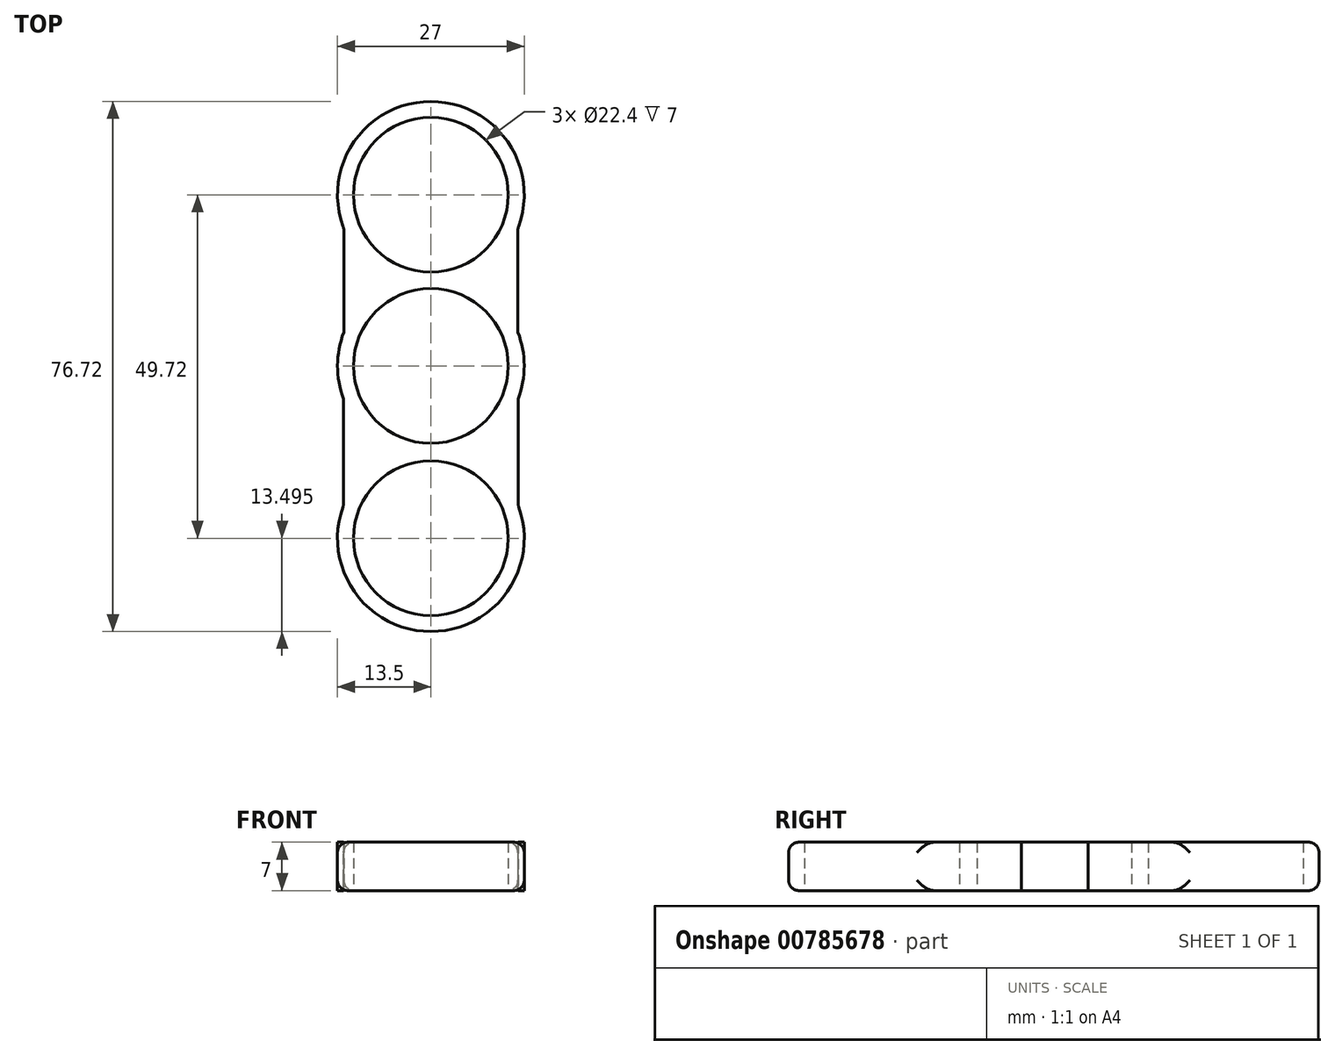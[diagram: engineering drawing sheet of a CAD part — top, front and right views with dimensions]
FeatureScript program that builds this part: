
annotation { "Feature Type Name" : "Feature", "Feature Type Description" : "" }
export const myFeature = defineFeature(function(context is Context, id is Id, definition is map)
    precondition{}
    {
        {
            var Q0;
            Q0=qCreatedBy(makeId("Top.planeOp"),FACE);
            var sketch = newSketch(context, id + "F0", { "sketchPlane" : qUnion([Q0])});
            skCircle(sketch, "E0", {"center": v(0, 0) * mm, "radius": 11.2 * mm});
            skArc(sketch, "E1", {"start": v(-12.59, 4.88) * mm, "mid": v(-13.5, 0.05) * mm, "end": v(-12.63, -4.77) * mm});
            skCircle(sketch, "E2", {"center": v(0, 24.79) * mm, "radius": 11.2 * mm});
            skArc(sketch, "E3", {"start": v(12.59, 19.91) * mm, "mid": v(0, 38.29) * mm, "end": v(-12.59, 19.91) * mm});
            skCircle(sketch, "E4", {"center": v(0, -24.93) * mm, "radius": 11.2 * mm});
            skArc(sketch, "E5", {"start": v(-12.63, -20.16) * mm, "mid": v(0, -38.43) * mm, "end": v(12.63, -20.16) * mm});
            skLineSegment(sketch, "E6", {"start": v(-12.59, 19.91) * mm, "end": v(-12.59, 4.88) * mm});
            skLineSegment(sketch, "E7", {"start": v(-12.63, -4.77) * mm, "end": v(-12.63, -20.16) * mm});
            skLineSegment(sketch, "E8", {"start": v(12.63, -20.16) * mm, "end": v(12.63, -4.77) * mm});
            skLineSegment(sketch, "E9", {"start": v(12.59, 19.91) * mm, "end": v(12.59, 4.88) * mm});
            skArc(sketch, "E10.trimOffspring", {"start": v(12.63, -4.77) * mm, "mid": v(13.5, 0.05) * mm, "end": v(12.59, 4.88) * mm});
            skSolve(sketch);
        }
        {
            var Q0;
            Q0=makeQuery(id+"F0.imprint","IMPRINT",FACE,{"disambiguationData":[TD([[makeQuery(id+"F0.imprint","IMPRINT",EDGE,{"derivedFrom":sQuery(id+"F0.wireOp",EDGE,"E0")}),-1.0]])]});
            extrude(context, id + "F1", {"entities" : qUnion([Q0]), "depth" : 7 * mm, "offsetDistance" : 25 * mm});
        }
        {
            var Q0;
            Q0=makeQuery(id+"F1.opExtrude","SWEPT_FACE",FACE,{"disambiguationData":[OSD([sQuery(id+"F0.wireOp",EDGE,"E3")])]});
            var Q1;
            Q1=makeQuery(id+"F1.opExtrude","SWEPT_FACE",FACE,{"disambiguationData":[OSD([sQuery(id+"F0.wireOp",EDGE,"E5")])]});
            fillet(context, id + "F2", {"entities" : qUnion([Q0, Q1]), "radius" : 1.5 * mm, "tangentPropagation" : true, "allowEdgeOverflow" : false});
        }
    });
